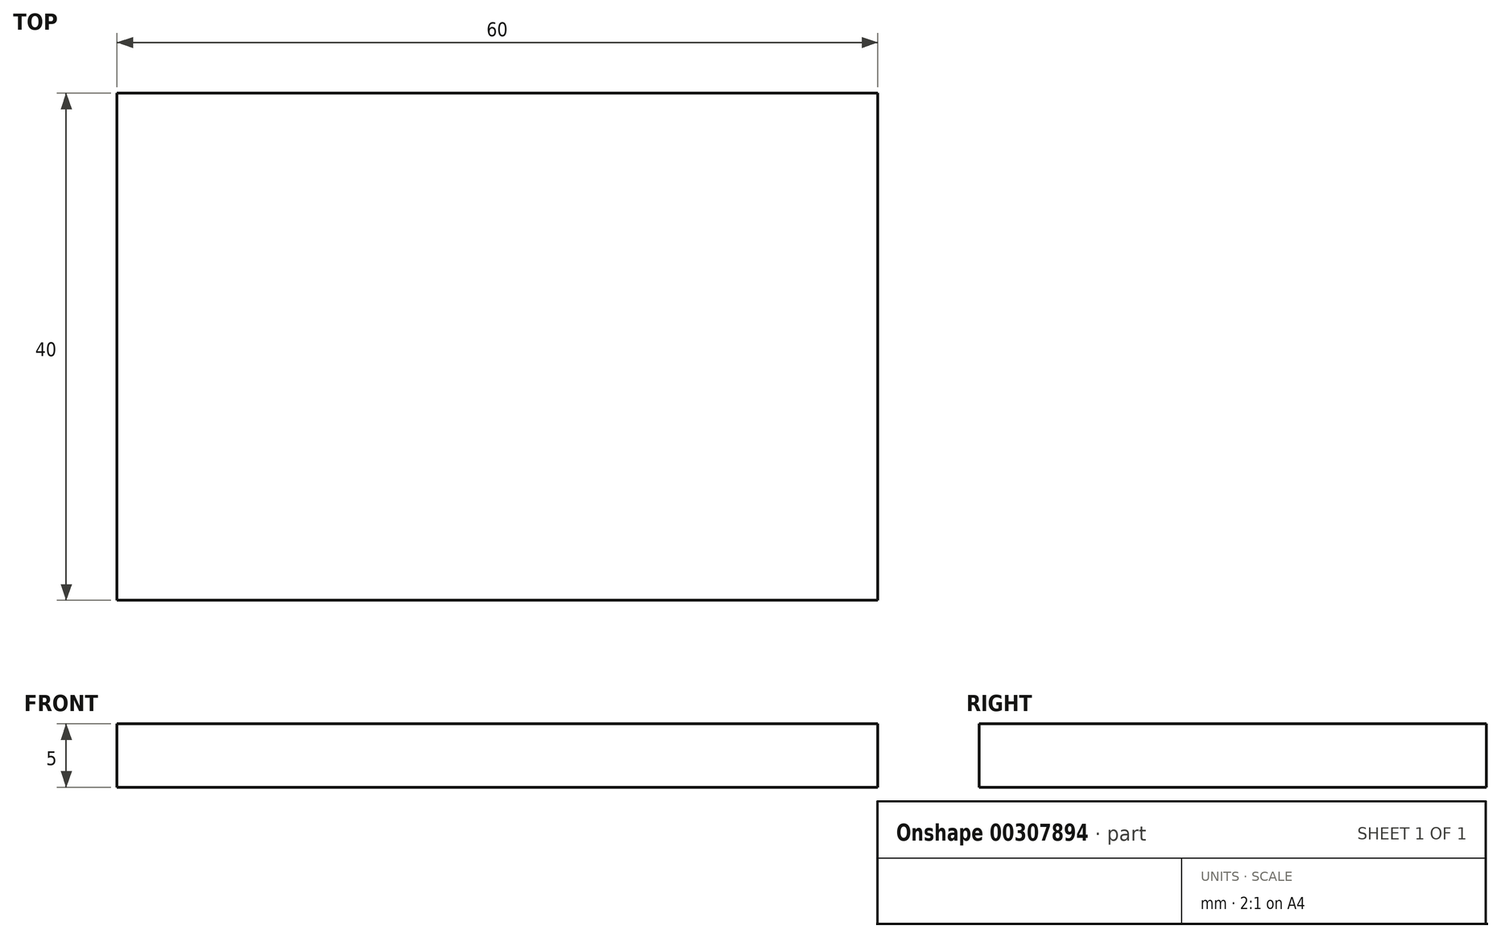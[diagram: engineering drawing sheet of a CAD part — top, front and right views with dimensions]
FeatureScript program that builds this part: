
annotation { "Feature Type Name" : "Feature", "Feature Type Description" : "" }
export const myFeature = defineFeature(function(context is Context, id is Id, definition is map)
    precondition{}
    {
        {
            var Q0;
            Q0=qCreatedBy(makeId("Top.planeOp"),FACE);
            var sketch = newSketch(context, id + "F0", { "sketchPlane" : qUnion([Q0])});
            skLineSegment(sketch, "E0.bottom", {"start": v(-30, 20) * mm, "end": v(30, 20) * mm});
            skLineSegment(sketch, "E0.top", {"start": v(-30, -20) * mm, "end": v(30, -20) * mm});
            skLineSegment(sketch, "E0.left", {"start": v(-30, 20) * mm, "end": v(-30, -20) * mm});
            skLineSegment(sketch, "E0.right", {"start": v(30, 20) * mm, "end": v(30, -20) * mm});
            skPoint(sketch, "E0.middle", {"position": v(0, 0) * mm});
            skSolve(sketch);
        }
        {
            var Q0;
            Q0 = qSketchRegion(id + "F0", true);
            extrude(context, id + "F1", {"entities" : qUnion([Q0]), "depth" : 5 * mm});
        }
    });
